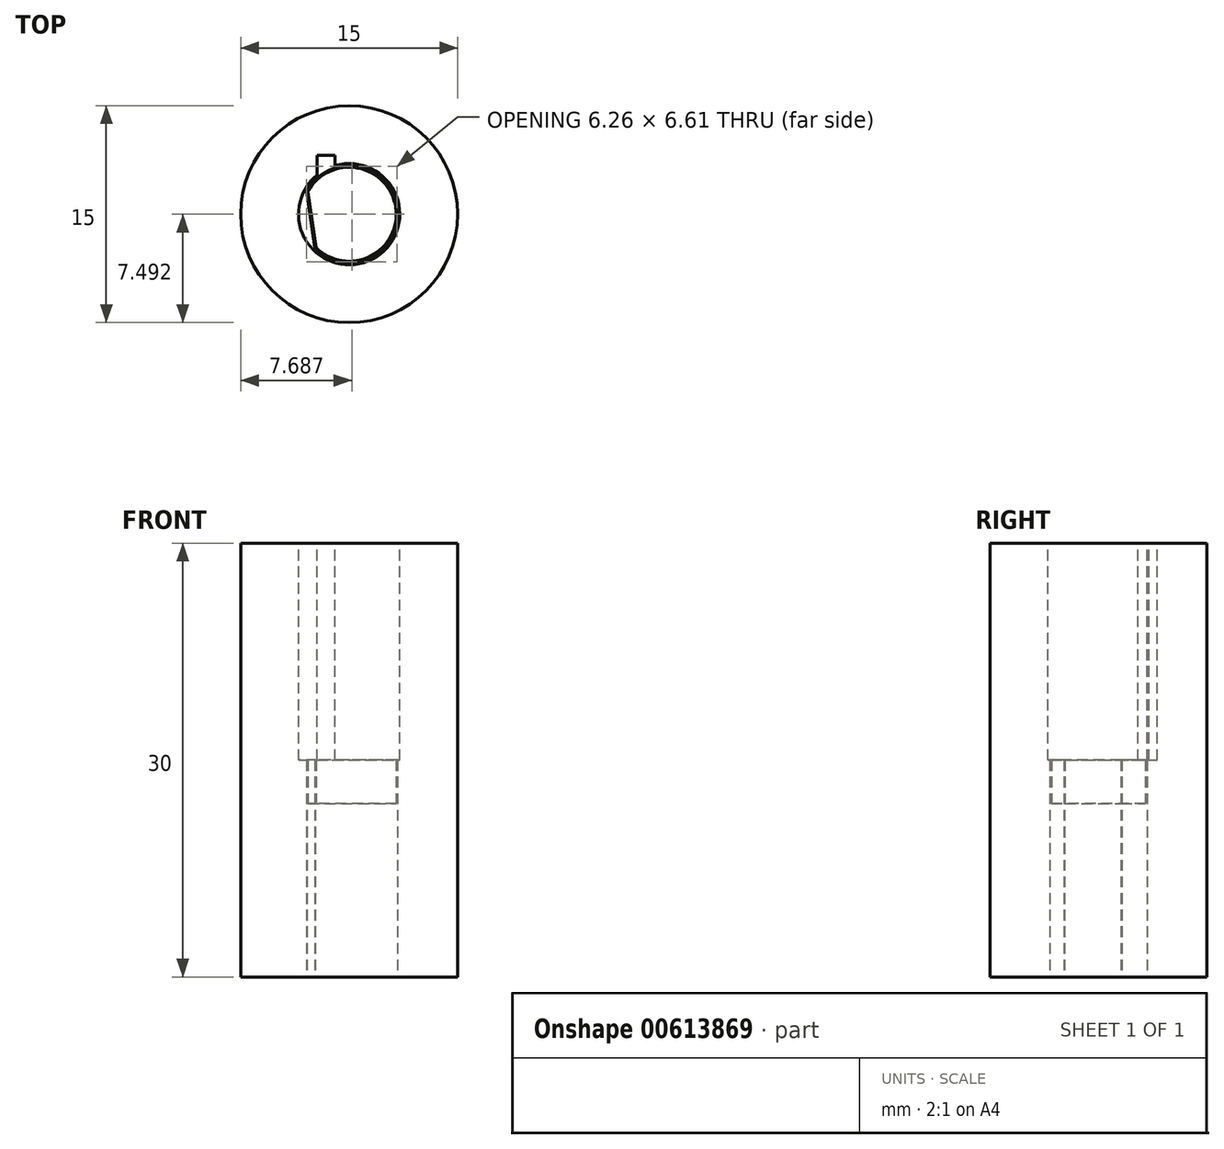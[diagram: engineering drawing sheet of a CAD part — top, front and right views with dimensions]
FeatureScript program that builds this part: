
annotation { "Feature Type Name" : "Feature", "Feature Type Description" : "" }
export const myFeature = defineFeature(function(context is Context, id is Id, definition is map)
    precondition{}
    {
        {
            var Q0;
            Q0=qCreatedBy(makeId("Top.planeOp"),FACE);
            var sketch = newSketch(context, id + "F0", { "sketchPlane" : qUnion([Q0])});
            skCircle(sketch, "E0", {"center": v(0, 0) * mm, "radius": 7.5 * mm});
            skSolve(sketch);
        }
        {
            var Q0;
            Q0=makeQuery(id+"F0.imprint","IMPRINT",FACE,{"disambiguationData":[TD([[makeQuery(id+"F0.imprint","IMPRINT",EDGE,{"derivedFrom":sQuery(id+"F0.wireOp",EDGE,"E0")}),1.0]])]});
            extrude(context, id + "F1", {"entities" : qUnion([Q0]), "depth" : 30 * mm, "offsetDistance" : 25 * mm});
        }
        {
            var Q0;
            Q0=makeQuery(id+"F1.opExtrude","CAP_FACE",FACE,{"disambiguationData":[OSD([sQuery(id+"F0.wireOp",EDGE,"E0")])],"isStart":false});
            var sketch = newSketch(context, id + "F2", { "sketchPlane" : qUnion([Q0])});
            skCircle(sketch, "E1", {"center": v(0, 0) * mm, "radius": 3.5 * mm});
            skSolve(sketch);
        }
        {
            var Q0;
            Q0=makeQuery(id+"F2.imprint","IMPRINT",FACE,{"disambiguationData":[TD([[makeQuery(id+"F2.imprint","IMPRINT",EDGE,{"derivedFrom":sQuery(id+"F2.wireOp",EDGE,"E1")}),1.0]])]});
            extrude(context, id + "F3", {"entities" : qUnion([Q0]), "operationType" : NewBodyOperationType.REMOVE, "oppositeDirection" : true, "depth" : 15 * mm, "offsetDistance" : 25 * mm});
        }
        {
            var Q0;
            Q0=makeQuery(id+"F1.opExtrude","CAP_FACE",FACE,{"disambiguationData":[OSD([sQuery(id+"F0.wireOp",EDGE,"E0")])],"isStart":true});
            var sketch = newSketch(context, id + "F4", { "sketchPlane" : qUnion([Q0])});
            skCircle(sketch, "E2", {"center": v(0, 0) * mm, "radius": 3.25 * mm});
            skLineSegment(sketch, "E3", {"start": v(-2.27, 2.32) * mm, "end": v(-2.84, -1.58) * mm});
            skSolve(sketch);
        }
        {
            var Q0;
            {var subQ0=sQuery(id+"F4.wireOp",EDGE,"E3");Q0=makeQuery(id+"F4.imprint","IMPRINT",FACE,{"disambiguationData":[TD([[makeQuery(id+"F4.imprint","IMPRINT",EDGE,{"derivedFrom":subQ0}),1.0]])]});}
            extrude(context, id + "F5", {"entities" : qUnion([Q0]), "operationType" : NewBodyOperationType.REMOVE, "oppositeDirection" : true, "depth" : 12 * mm, "offsetDistance" : 25 * mm});
        }
        {
            var Q0;
            Q0=makeQuery(id+"F1.opExtrude","CAP_FACE",FACE,{"disambiguationData":[OSD([sQuery(id+"F0.wireOp",EDGE,"E0")])],"isStart":false});
            var sketch = newSketch(context, id + "F6", { "sketchPlane" : qUnion([Q0])});
            skLineSegment(sketch, "E4.bottom", {"start": v(-2.2, 2.72) * mm, "end": v(-0.97, 2.72) * mm});
            skLineSegment(sketch, "E4.top", {"start": v(-2.2, 4.08) * mm, "end": v(-0.97, 4.08) * mm});
            skLineSegment(sketch, "E4.left", {"start": v(-2.2, 2.72) * mm, "end": v(-2.2, 4.08) * mm});
            skLineSegment(sketch, "E4.right", {"start": v(-0.97, 2.72) * mm, "end": v(-0.97, 4.08) * mm});
            skSolve(sketch);
        }
        {
            var Q0;
            {var subQ0=sQuery(id+"F6.wireOp",EDGE,"E4.top");Q0=makeQuery(id+"F6.imprint","IMPRINT",FACE,{"disambiguationData":[TD([[makeQuery(id+"F6.imprint","IMPRINT",EDGE,{"derivedFrom":subQ0}),-1.0]])]});}
            extrude(context, id + "F7", {"entities" : qUnion([Q0]), "operationType" : NewBodyOperationType.REMOVE, "oppositeDirection" : true, "depth" : 12 * mm, "offsetDistance" : 25 * mm});
        }
        {
            var Q0;
            Q0=makeQuery(id+"F7.boolean.opBoolean","COPY",FACE,{"derivedFrom":makeQuery(id+"F7.opExtrude","CAP_FACE",FACE,{"disambiguationData":[OSD([sQuery(id+"F2.wireOp",EDGE,"E1"),sQuery(id+"F6.wireOp",EDGE,"E4.top"),sQuery(id+"F6.wireOp",EDGE,"E4.left"),sQuery(id+"F6.wireOp",EDGE,"E4.right")])],"isStart":false})});
            extrude(context, id + "F8", {"entities" : qUnion([Q0]), "operationType" : NewBodyOperationType.REMOVE, "oppositeDirection" : true, "depth" : 3 * mm, "offsetDistance" : 25 * mm});
        }
        {
            var Q0;
            Q0=makeQuery(id+"F1.opExtrude","CAP_FACE",FACE,{"disambiguationData":[OSD([sQuery(id+"F0.wireOp",EDGE,"E0")])],"isStart":true});
            var sketch = newSketch(context, id + "F9", { "sketchPlane" : qUnion([Q0])});
            skArc(sketch, "E5.0", {"start": v(-2.93, -1.63) * mm, "mid": v(3.31, -0.48) * mm, "end": v(-2.34, 2.4) * mm});
            skLineSegment(sketch, "E6.0", {"start": v(-2.37, 2.34) * mm, "end": v(-2.94, -1.56) * mm});
            skLineSegment(sketch, "E7", {"start": v(-2.34, 2.4) * mm, "end": v(-2.37, 2.34) * mm});
            skLineSegment(sketch, "E8", {"start": v(-2.94, -1.56) * mm, "end": v(-2.93, -1.63) * mm});
            skSolve(sketch);
        }
        {
            var Q0;
            Q0=makeQuery(id+"F9.imprint","IMPRINT",FACE,{"disambiguationData":[TD([[makeQuery(id+"F9.imprint","IMPRINT",EDGE,{"derivedFrom":sQuery(id+"F9.wireOp",EDGE,"E5.0")}),1.0]])]});
            extrude(context, id + "F10", {"entities" : qUnion([Q0]), "operationType" : NewBodyOperationType.REMOVE, "endBound" : BoundingType.UP_TO_NEXT, "oppositeDirection" : true, "depth" : 25 * mm, "offsetDistance" : 25 * mm});
        }
    });
